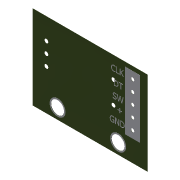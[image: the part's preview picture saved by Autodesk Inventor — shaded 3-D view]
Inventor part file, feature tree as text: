
AUTODESK INVENTOR PART (.ipt)
format: ipt  version: 2014 (Build 180170000, 170)  size: 373,248 bytes
history: native  units: in
note: dims shown in document units (in); Inventor stores cm internally (conversion verified against a paired STEP export)
features: reference x8, extrude x3, sketch x2
ambient origin geometry x8: Origin, YZ Plane, XZ Plane, XY Plane, X Axis, Y Axis, Z Axis, Center Point
bodies: Solid1 (feature_tree)
feature tree (13):
  extrude  "Extrusion1"  Depth=0.14in
  extrude  "Extrusion2"  Depth=0.001in
  extrude  "Extrusion3"  Depth=0.001in
  sketch  "Sketch3"  dims[d0=0.14in d1=0.14in]
  reference  "Reference1"
  sketch  "Sketch4"  dims[d2=0.13in d3=0.53in d4=0.4in d5=0.53in d7=0.1in d8=0.1in d9=0.1in d10=0.1in d11=0.065in d12=0.001in d13=0.0in d14=0.135in d15=0.53in d16=0.0675in d17=0.065in d18=0.4in d19=0.143in d20=0.001in d21=0.0in d22=0.035in d23=0.035in d24=0.001in d25=0.0in d26=0.0in d27=0.1in d28=0.1in]
  reference  "Reference2"
  reference  "Reference3"
  reference  "Reference4"
  reference  "Reference5"
  reference  "Reference6"
  reference  "Reference7"
  reference  "Reference8"
